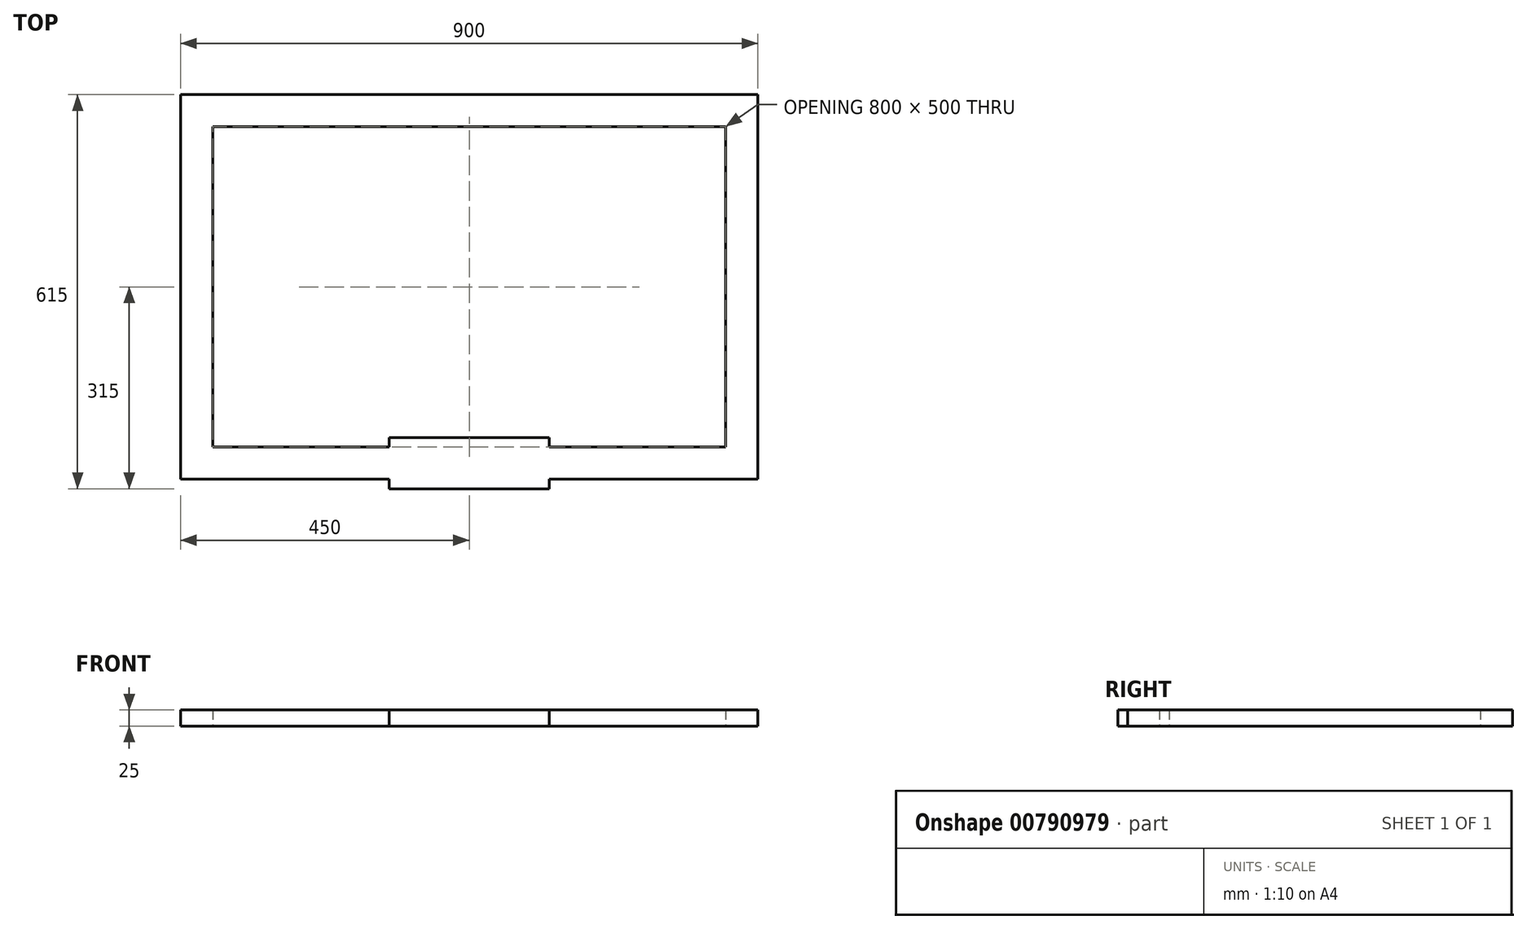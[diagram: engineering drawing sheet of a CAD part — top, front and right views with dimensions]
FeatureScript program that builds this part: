
annotation { "Feature Type Name" : "Feature", "Feature Type Description" : "" }
export const myFeature = defineFeature(function(context is Context, id is Id, definition is map)
    precondition{}
    {
        {
            var Q0;
            Q0=qCreatedBy(makeId("Top.planeOp"),FACE);
            var sketch = newSketch(context, id + "F0", { "sketchPlane" : qUnion([Q0])});
            skLineSegment(sketch, "E0", {"start": v(0, 0) * mm, "end": v(900, 0) * mm});
            skLineSegment(sketch, "E1", {"start": v(900, 0) * mm, "end": v(900, -600) * mm});
            skLineSegment(sketch, "E2", {"start": v(900, -600) * mm, "end": v(575, -600) * mm});
            skLineSegment(sketch, "E3", {"start": v(0, 0) * mm, "end": v(0, -600) * mm});
            skLineSegment(sketch, "E4.0", {"start": v(50, -50) * mm, "end": v(50, -550) * mm});
            skLineSegment(sketch, "E4.1", {"start": v(50, -50) * mm, "end": v(850, -50) * mm});
            skLineSegment(sketch, "E4.2", {"start": v(850, -50) * mm, "end": v(850, -550) * mm});
            skLineSegment(sketch, "E4.3", {"start": v(850, -550) * mm, "end": v(575, -550) * mm});
            skLineSegment(sketch, "E5.bottom", {"start": v(0, -600) * mm, "end": v(325, -600) * mm});
            skLineSegment(sketch, "E5.top", {"start": v(0, -550) * mm, "end": v(325, -550) * mm});
            skLineSegment(sketch, "E5.left", {"start": v(0, -600) * mm, "end": v(0, -550) * mm});
            skPoint(sketch, "E6.oppositeSnap0", {"position": v(450, -575) * mm});
            skPoint(sketch, "E6.top.end.orphan", {"position": v(433.63, -575) * mm});
            skLineSegment(sketch, "E7.bottom", {"start": v(575, -535) * mm, "end": v(325, -535) * mm});
            skLineSegment(sketch, "E7.top", {"start": v(575, -615) * mm, "end": v(325, -615) * mm});
            skLineSegment(sketch, "E7.left", {"start": v(575, -535) * mm, "end": v(575, -615) * mm});
            skLineSegment(sketch, "E7.right", {"start": v(325, -535) * mm, "end": v(325, -615) * mm});
            skLineSegment(sketch, "E8.trimOffspring", {"start": v(325, -550) * mm, "end": v(50, -550) * mm});
            skPoint(sketch, "E9.orphan", {"position": v(450, -550) * mm});
            skLineSegment(sketch, "E10.trimOffspring", {"start": v(325, -600) * mm, "end": v(0, -600) * mm});
            skLineSegment(sketch, "E11.trimOffspring", {"start": v(450, -600) * mm, "end": v(435.75, -600) * mm});
            skSolve(sketch);
        }
        {
            var Q0;
            Q0 = qSketchRegion(id + "F0", true);
            extrude(context, id + "F1", {"entities" : qUnion([Q0]), "depth" : 25 * mm, "offsetDistance" : 25 * mm});
        }
    });
